SOLIDWORKS PART (.sldprt)
format: sldprt  version: not decoded by parser v0  size: 957,440 bytes
history: native  units: mm
features: extrude x7, sketch x4, plane x3, material x1 (+8 scaffold rows collapsed)
feature tree (23):
  scaffold x8  (default folders/planes/origin — collapsed)
  material  "Material <not specified>"
  plane  "Alzado"
  plane  "Planta"
  plane  "Vista lateral"
  sketch  "Croquis1"  dims[D1=0.5mm D2=0.5mm D3=90.0deg D4=2.54mm D5=2.54mm]
  extrude  "Extruir1"  Depth=0mm PW2_UID_val=0mm
  sketch  "Croquis2"  dims[D1=7.5mm D2=0.5mm D3=2.25mm D4=2.54mm]
  extrude  "Extruir2"  [1 undecoded]
  extrude  "pw2 (4)"  Depth=0mm PW2_UID_val=0mm
  sketch  "Croquis3"  dims[D1=0.9mm D2=0.9mm D3=0.9mm D4=0.9mm D5=0.8mm D6=45.0deg D7=0.8mm D8=45.0deg D9=0.8mm D10=45.0deg D11=0.8mm D12=45.0deg D13=2.54mm D14=2.54mm]
  extrude  "Extruir4"  [1 undecoded]
  extrude  "pw2 (1)"  Depth=0mm PW2_UID_val=0mm
  sketch  "Croquis4"
  extrude  "Extruir5"  [1 undecoded]
  extrude  "pw2 (2)"  Depth=0mm PW2_UID_val=0mm
decode coverage: 7 of 11 modeling features carry decoded parameters
note: 3 parameter values undecoded
summary: no parameter record found for 3 features
note: suppression state not decoded; provenance and decode notes live in map.json
